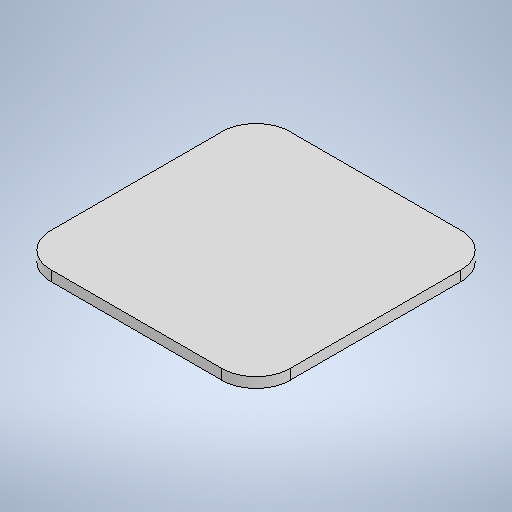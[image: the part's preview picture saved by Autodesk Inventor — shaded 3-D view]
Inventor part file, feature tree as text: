
AUTODESK INVENTOR PART (.ipt)
format: ipt  version: 2025 (Build 290162010, 162A)  size: 250,368 bytes
history: native  units: mm
features: other x2, sheet_metal_op x1, chamfer x1, sketch x1
ambient origin geometry x8: Origin, YZ Plane, XZ Plane, XY Plane, X Axis, Y Axis, Z Axis, Center Point
bodies: Solid1 (feature_tree)
feature tree (5):
  sheet_metal_op  "Face1"
  chamfer  "Corner Round1"
  sketch  "Sketch1"  dims[d0=140.0mm d1=140.0mm d2=6.0mm d22=20.0mm]
  other  "Plate1"
  other  "Definition1"
